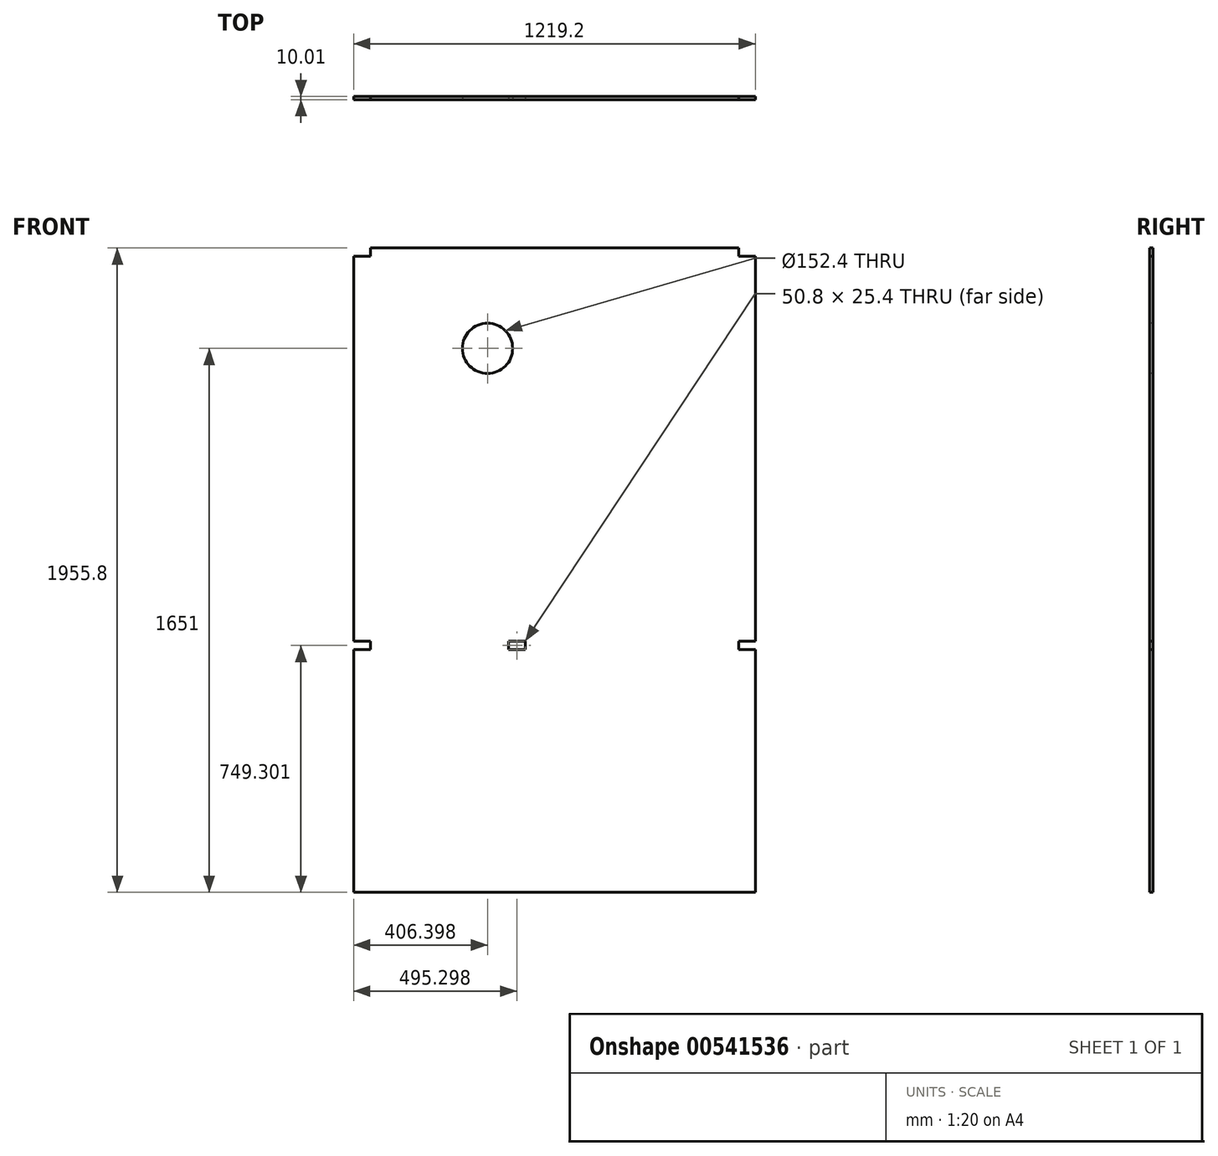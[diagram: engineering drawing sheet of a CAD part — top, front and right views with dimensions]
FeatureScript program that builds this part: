
annotation { "Feature Type Name" : "Feature", "Feature Type Description" : "" }
export const myFeature = defineFeature(function(context is Context, id is Id, definition is map)
    precondition{}
    {
        {
            var Q0;
            Q0=qCreatedBy(makeId("Front.planeOp"),FACE);
            var sketch = newSketch(context, id + "F0", { "sketchPlane" : qUnion([Q0])});
            skLineSegment(sketch, "E0", {"start": v(-507.77, 899.2) * mm, "end": v(711.43, 899.2) * mm});
            skLineSegment(sketch, "E1", {"start": v(711.43, 899.2) * mm, "end": v(711.43, -320) * mm});
            skLineSegment(sketch, "E2", {"start": v(711.43, -320) * mm, "end": v(711.17, -320) * mm});
            skLineSegment(sketch, "E3", {"start": v(711.17, -320) * mm, "end": v(711.17, -1056.6) * mm});
            skLineSegment(sketch, "E4", {"start": v(711.17, -1056.6) * mm, "end": v(-507.77, -1056.6) * mm});
            skLineSegment(sketch, "E5", {"start": v(-507.77, -1056.6) * mm, "end": v(-507.77, 899.2) * mm});
            skSolve(sketch);
        }
        {
            var Q0;
            Q0=qSketchRegion(id+"F0",true);
            extrude(context, id + "F1", {"entities" : qUnion([Q0]), "depth" : 10 * mm, "offsetDistance" : 25.4 * mm});
        }
        {
            var Q0;
            Q0=makeQuery(id+"F1.opExtrude","CAP_FACE",FACE,{"disambiguationData":[OSD([sQuery(id+"F0.wireOp",EDGE,"E0"),sQuery(id+"F0.wireOp",EDGE,"E1"),sQuery(id+"F0.wireOp",EDGE,"E2"),sQuery(id+"F0.wireOp",EDGE,"E3"),sQuery(id+"F0.wireOp",EDGE,"E4"),sQuery(id+"F0.wireOp",EDGE,"E5")])],"isStart":false});
            var sketch = newSketch(context, id + "F2", { "sketchPlane" : qUnion([Q0])});
            skLineSegment(sketch, "E6.bottom", {"start": v(660.63, 873.8) * mm, "end": v(711.43, 873.8) * mm});
            skLineSegment(sketch, "E6.top", {"start": v(660.63, 899.2) * mm, "end": v(711.43, 899.2) * mm});
            skLineSegment(sketch, "E6.left", {"start": v(660.63, 873.8) * mm, "end": v(660.63, 899.2) * mm});
            skLineSegment(sketch, "E6.right", {"start": v(711.43, 873.8) * mm, "end": v(711.43, 899.2) * mm});
            skLineSegment(sketch, "E7.bottom", {"start": v(-456.97, 873.8) * mm, "end": v(-507.77, 873.8) * mm});
            skLineSegment(sketch, "E7.top", {"start": v(-456.97, 899.2) * mm, "end": v(-507.77, 899.2) * mm});
            skLineSegment(sketch, "E7.left", {"start": v(-456.97, 873.8) * mm, "end": v(-456.97, 899.2) * mm});
            skLineSegment(sketch, "E7.right", {"start": v(-507.77, 873.8) * mm, "end": v(-507.77, 899.2) * mm});
            skLineSegment(sketch, "E8.bottom", {"start": v(660.63, -294.6) * mm, "end": v(711.43, -294.6) * mm});
            skLineSegment(sketch, "E8.top", {"start": v(660.63, -320) * mm, "end": v(711.43, -320) * mm});
            skLineSegment(sketch, "E8.left", {"start": v(660.63, -294.6) * mm, "end": v(660.63, -320) * mm});
            skLineSegment(sketch, "E8.right", {"start": v(711.43, -294.6) * mm, "end": v(711.43, -320) * mm});
            skLineSegment(sketch, "E9.bottom", {"start": v(-507.77, -320) * mm, "end": v(-456.97, -320) * mm});
            skLineSegment(sketch, "E9.top", {"start": v(-507.77, -294.6) * mm, "end": v(-456.97, -294.6) * mm});
            skLineSegment(sketch, "E9.left", {"start": v(-507.77, -320) * mm, "end": v(-507.77, -294.6) * mm});
            skLineSegment(sketch, "E9.right", {"start": v(-456.97, -320) * mm, "end": v(-456.97, -294.6) * mm});
            skLineSegment(sketch, "E10.bottom", {"start": v(-37.87, -320) * mm, "end": v(12.93, -320) * mm});
            skLineSegment(sketch, "E10.top", {"start": v(-37.87, -294.6) * mm, "end": v(12.93, -294.6) * mm});
            skLineSegment(sketch, "E10.left", {"start": v(-37.87, -320) * mm, "end": v(-37.87, -294.6) * mm});
            skLineSegment(sketch, "E10.right", {"start": v(12.93, -320) * mm, "end": v(12.93, -294.6) * mm});
            skSolve(sketch);
        }
        {
            var Q0;
            Q0=qSketchRegion(id+"F2",true);
            extrude(context, id + "F3", {"entities" : qUnion([Q0]), "operationType" : NewBodyOperationType.REMOVE, "endBound" : BoundingType.THROUGH_ALL, "oppositeDirection" : true, "depth" : 25.4 * mm, "offsetDistance" : 25.4 * mm});
        }
        {
            var Q0;
            Q0=makeQuery(id+"F1.opExtrude","CAP_FACE",FACE,{"disambiguationData":[OSD([sQuery(id+"F0.wireOp",EDGE,"E0"),sQuery(id+"F0.wireOp",EDGE,"E1"),sQuery(id+"F0.wireOp",EDGE,"E2"),sQuery(id+"F0.wireOp",EDGE,"E3"),sQuery(id+"F0.wireOp",EDGE,"E4"),sQuery(id+"F0.wireOp",EDGE,"E5")])],"isStart":false});
            var sketch = newSketch(context, id + "F4", { "sketchPlane" : qUnion([Q0])});
            skCircle(sketch, "E11", {"center": v(-101.37, 594.4) * mm, "radius": 76.2 * mm});
            skSolve(sketch);
        }
        {
            var Q0;
            Q0=qSketchRegion(id+"F4",true);
            extrude(context, id + "F5", {"entities" : qUnion([Q0]), "operationType" : NewBodyOperationType.REMOVE, "endBound" : BoundingType.THROUGH_ALL, "oppositeDirection" : true, "depth" : 25.4 * mm, "offsetDistance" : 25.4 * mm});
        }
    });
